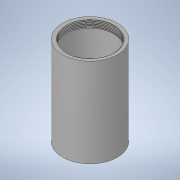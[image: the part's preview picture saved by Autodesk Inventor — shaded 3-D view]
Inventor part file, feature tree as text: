
AUTODESK INVENTOR PART (.ipt)
format: ipt  version: 2021.2 (Build 252289000, 289)  size: 283,648 bytes
history: imported  units: in
note: dims shown in document units (in); Inventor stores cm internally (conversion verified against a paired STEP export)
features: imported_body x1
ambient origin geometry x8: Origin, YZ Plane, XZ Plane, XY Plane, X Axis, Y Axis, Z Axis, Center Point
bodies: Solid1 (imported_parasolid), Body1 (imported_parasolid)
feature tree (1):
  imported_body  NMx_Import_Brep_tag  [imported B-rep: ~6 faces, bbox_mm=None]
